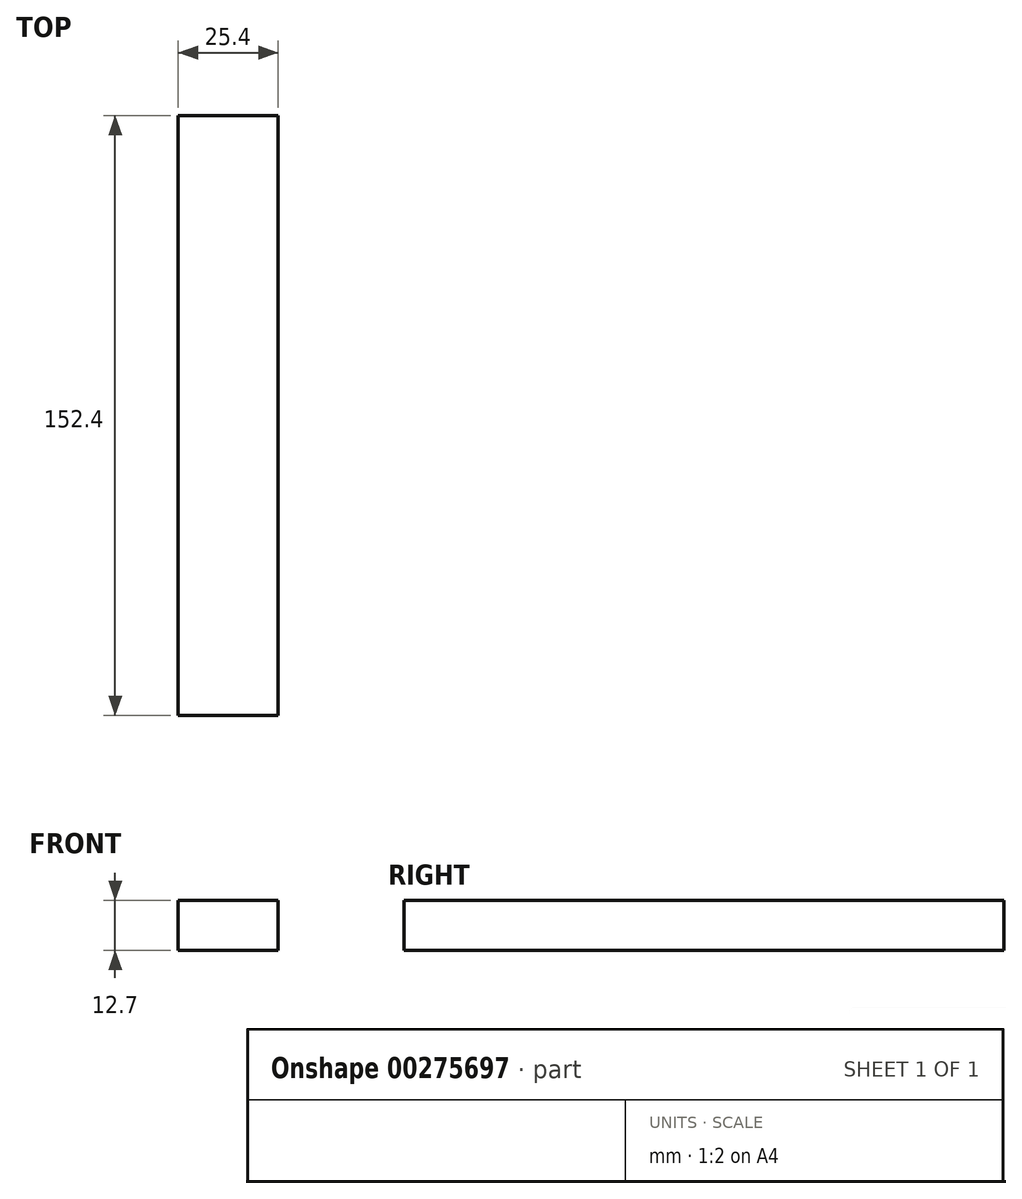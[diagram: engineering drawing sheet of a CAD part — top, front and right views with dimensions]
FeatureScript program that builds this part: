
annotation { "Feature Type Name" : "Feature", "Feature Type Description" : "" }
export const myFeature = defineFeature(function(context is Context, id is Id, definition is map)
    precondition{}
    {
        {
            var Q0;
            Q0=qCreatedBy(makeId("Front.planeOp"),FACE);
            var sketch = newSketch(context, id + "F0", { "sketchPlane" : qUnion([Q0])});
            skLineSegment(sketch, "E0.bottom", {"start": v(-55.07, 0) * mm, "end": v(-29.67, 0) * mm});
            skLineSegment(sketch, "E0.top", {"start": v(-55.07, -12.7) * mm, "end": v(-29.67, -12.7) * mm});
            skLineSegment(sketch, "E0.left", {"start": v(-55.07, 0) * mm, "end": v(-55.07, -12.7) * mm});
            skLineSegment(sketch, "E0.right", {"start": v(-29.67, 0) * mm, "end": v(-29.67, -12.7) * mm});
            skSolve(sketch);
        }
        {
            var Q0;
            Q0=makeQuery(id+"F0.imprint","IMPRINT",FACE,{"disambiguationData":[TD([[makeQuery(id+"F0.imprint","IMPRINT",EDGE,{"derivedFrom":sQuery(id+"F0.wireOp",EDGE,"E0.bottom")}),-1.0]])]});
            extrude(context, id + "F1", {"entities" : qUnion([Q0]), "depth" : 152.4 * mm});
        }
    });
